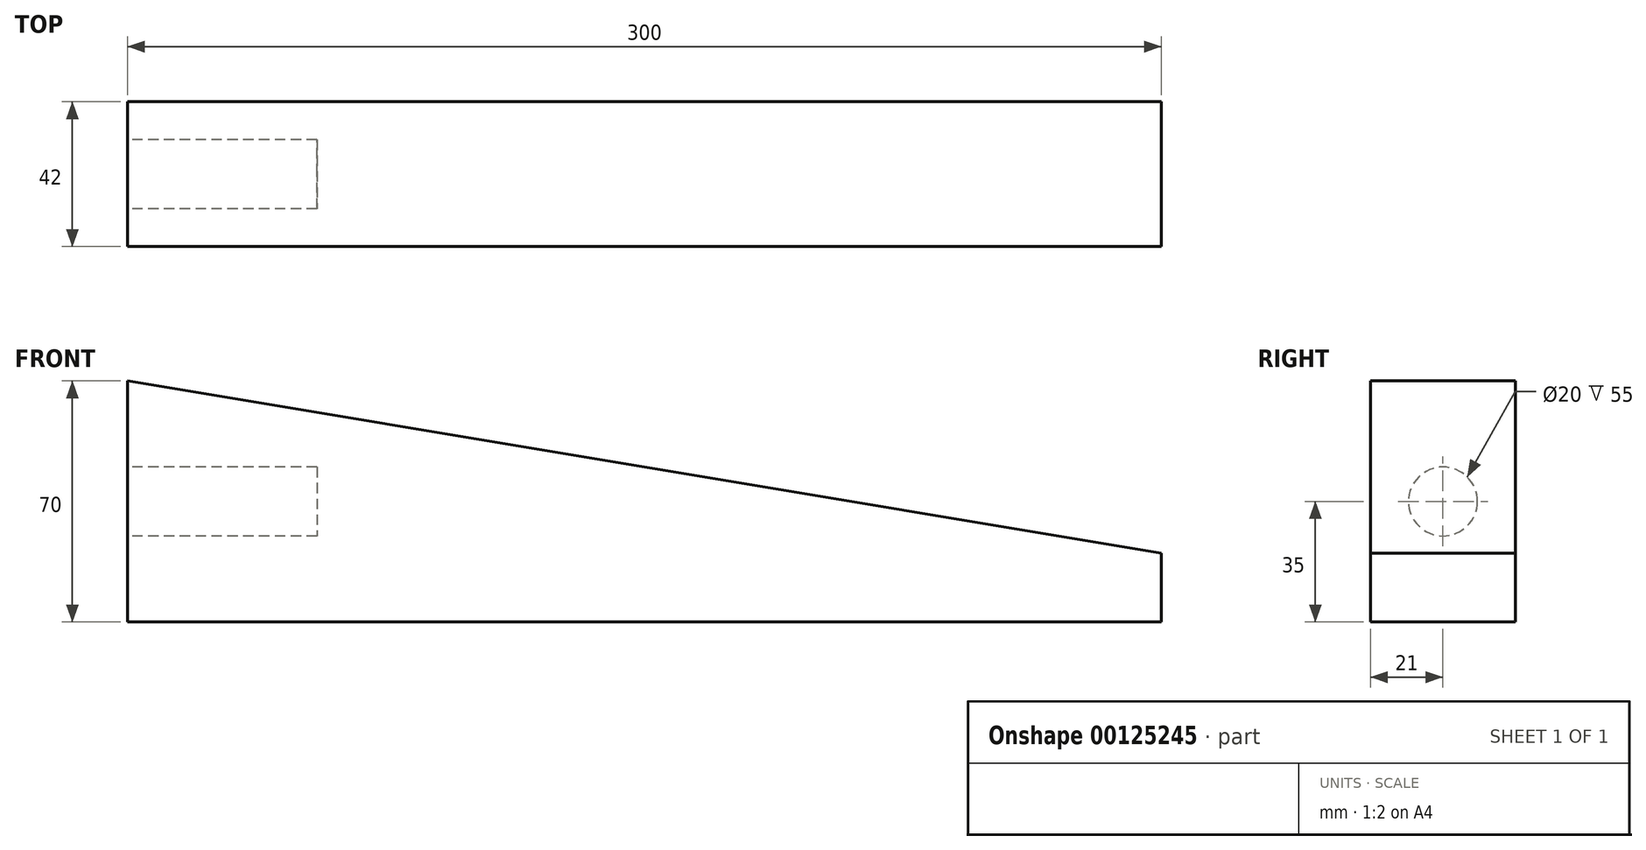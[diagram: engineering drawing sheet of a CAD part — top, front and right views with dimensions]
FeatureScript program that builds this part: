
annotation { "Feature Type Name" : "Feature", "Feature Type Description" : "" }
export const myFeature = defineFeature(function(context is Context, id is Id, definition is map)
    precondition{}
    {
        {
            var Q0;
            Q0=qCreatedBy(makeId("Front.planeOp"),FACE);
            var sketch = newSketch(context, id + "F0", { "sketchPlane" : qUnion([Q0])});
            skLineSegment(sketch, "E0", {"start": v(0, 0) * mm, "end": v(300, 0) * mm});
            skLineSegment(sketch, "E1", {"start": v(300, 0) * mm, "end": v(300, 20) * mm});
            skLineSegment(sketch, "E2", {"start": v(300, 20) * mm, "end": v(0, 70) * mm});
            skLineSegment(sketch, "E3", {"start": v(0, 70) * mm, "end": v(0, 0) * mm});
            skSolve(sketch);
        }
        {
            var Q0;
            Q0=makeQuery(id+"F0.imprint","IMPRINT",FACE,{"disambiguationData":[TD([[makeQuery(id+"F0.imprint","IMPRINT",EDGE,{"derivedFrom":sQuery(id+"F0.wireOp",EDGE,"E0")}),1.0]])]});
            extrude(context, id + "F1", {"entities" : qUnion([Q0]), "depth" : 42 * mm});
        }
        {
            var Q0;
            Q0=makeQuery(id+"F1.opExtrude","SWEPT_FACE",FACE,{"disambiguationData":[OSD([sQuery(id+"F0.wireOp",EDGE,"E3")])]});
            var sketch = newSketch(context, id + "F2", { "sketchPlane" : qUnion([Q0])});
            skCircle(sketch, "E4", {"center": v(21, 35) * mm, "radius": 10 * mm});
            skPoint(sketch, "E4.centerSnap0", {"position": v(21, 70) * mm});
            skSolve(sketch);
        }
        {
            var Q0;
            Q0=makeQuery(id+"F2.imprint","IMPRINT",FACE,{"disambiguationData":[TD([[makeQuery(id+"F2.imprint","IMPRINT",EDGE,{"derivedFrom":sQuery(id+"F2.wireOp",EDGE,"E4")}),1.0]])]});
            extrude(context, id + "F3", {"entities" : qUnion([Q0]), "operationType" : NewBodyOperationType.REMOVE, "oppositeDirection" : true, "depth" : 55 * mm});
        }
    });
